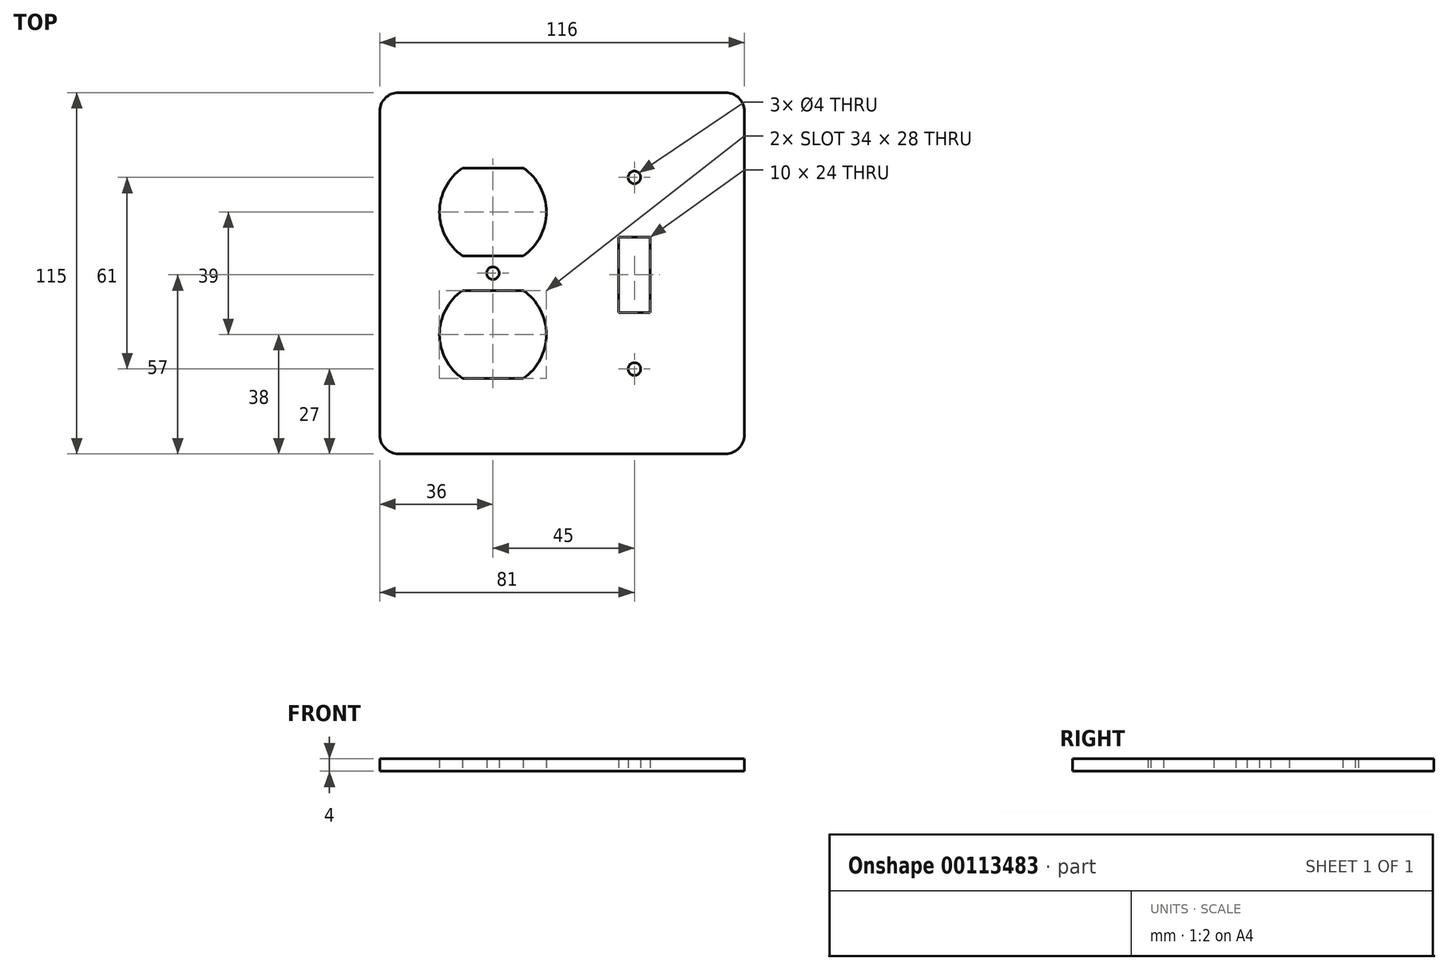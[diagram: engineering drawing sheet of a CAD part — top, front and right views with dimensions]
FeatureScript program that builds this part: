
annotation { "Feature Type Name" : "Feature", "Feature Type Description" : "" }
export const myFeature = defineFeature(function(context is Context, id is Id, definition is map)
    precondition{}
    {
        {
            var Q0;
            Q0=qCreatedBy(makeId("Top.planeOp"),FACE);
            var sketch = newSketch(context, id + "F0", { "sketchPlane" : qUnion([Q0])});
            skLineSegment(sketch, "E0.bottom", {"start": v(0, 0) * mm, "end": v(116, 0) * mm});
            skLineSegment(sketch, "E0.top", {"start": v(0, 115) * mm, "end": v(116, 115) * mm});
            skLineSegment(sketch, "E0.left", {"start": v(0, 0) * mm, "end": v(0, 115) * mm});
            skLineSegment(sketch, "E0.right", {"start": v(116, 0) * mm, "end": v(116, 115) * mm});
            skLineSegment(sketch, "E1.bottom", {"start": v(76, 69) * mm, "end": v(86, 69) * mm});
            skLineSegment(sketch, "E1.top", {"start": v(76, 45) * mm, "end": v(86, 45) * mm});
            skLineSegment(sketch, "E1.left", {"start": v(76, 69) * mm, "end": v(76, 45) * mm});
            skLineSegment(sketch, "E1.right", {"start": v(86, 69) * mm, "end": v(86, 45) * mm});
            skCircle(sketch, "E2", {"center": v(81, 88) * mm, "radius": 2 * mm});
            skCircle(sketch, "E3", {"center": v(81, 27) * mm, "radius": 2 * mm});
            skLineSegment(sketch, "E4.direction1", {"start": v(81, 27) * mm, "end": v(35, 27) * mm, "construction": true});
            skSolve(sketch);
        }
        {
            var Q0;
            Q0=qSketchRegion(id+"F0",true);
            extrude(context, id + "F1", {"entities" : qUnion([Q0]), "depth" : 4 * mm});
        }
        {
            var Q0;
            Q0=makeQuery(id+"F1.opExtrude","SWEPT_EDGE",EDGE,{"disambiguationData":[OSD([sQuery(id+"F0.wireOp",EDGE,"E0.top"),sQuery(id+"F0.wireOp",EDGE,"E0.left")])]});
            var Q1;
            Q1=makeQuery(id+"F1.opExtrude","SWEPT_EDGE",EDGE,{"disambiguationData":[OSD([sQuery(id+"F0.wireOp",EDGE,"E0.top"),sQuery(id+"F0.wireOp",EDGE,"E0.right")])]});
            var Q2;
            Q2=makeQuery(id+"F1.opExtrude","SWEPT_EDGE",EDGE,{"disambiguationData":[OSD([sQuery(id+"F0.wireOp",EDGE,"E0.bottom"),sQuery(id+"F0.wireOp",EDGE,"E0.right")])]});
            var Q3;
            Q3=makeQuery(id+"F1.opExtrude","SWEPT_EDGE",EDGE,{"disambiguationData":[OSD([sQuery(id+"F0.wireOp",EDGE,"E0.bottom"),sQuery(id+"F0.wireOp",EDGE,"E0.left")])]});
            fillet(context, id + "F2", {"entities" : qUnion([Q0, Q1, Q2, Q3]), "radius" : 6 * mm, "tangentPropagation" : true, "allowEdgeOverflow" : false});
        }
        {
            var Q0;
            Q0=makeQuery(id+"F1.opExtrude","CAP_FACE",FACE,{"disambiguationData":[OSD([sQuery(id+"F0.wireOp",EDGE,"E0.bottom"),sQuery(id+"F0.wireOp",EDGE,"E0.top"),sQuery(id+"F0.wireOp",EDGE,"E0.left"),sQuery(id+"F0.wireOp",EDGE,"E0.right"),sQuery(id+"F0.wireOp",EDGE,"E1.bottom"),sQuery(id+"F0.wireOp",EDGE,"E1.top"),sQuery(id+"F0.wireOp",EDGE,"E1.left"),sQuery(id+"F0.wireOp",EDGE,"E1.right"),sQuery(id+"F0.wireOp",EDGE,"E2"),sQuery(id+"F0.wireOp",EDGE,"E3")])],"isStart":false});
            var sketch = newSketch(context, id + "F3", { "sketchPlane" : qUnion([Q0])});
            skLineSegment(sketch, "E5.0.0", {"start": v(0, 109) * mm, "end": v(0, 6) * mm});
            skArc(sketch, "E5.0.1", {"start": v(0, 6) * mm, "mid": v(1.76, 1.76) * mm, "end": v(6, 0) * mm});
            skLineSegment(sketch, "E5.0.2", {"start": v(6, 0) * mm, "end": v(110, 0) * mm});
            skArc(sketch, "E5.0.3", {"start": v(110, 0) * mm, "mid": v(114.24, 1.76) * mm, "end": v(116, 6) * mm});
            skLineSegment(sketch, "E5.0.4", {"start": v(116, 6) * mm, "end": v(116, 109) * mm});
            skArc(sketch, "E5.0.5", {"start": v(116, 109) * mm, "mid": v(114.24, 113.24) * mm, "end": v(110, 115) * mm});
            skLineSegment(sketch, "E5.0.6", {"start": v(110, 115) * mm, "end": v(6, 115) * mm});
            skArc(sketch, "E5.0.7", {"start": v(6, 115) * mm, "mid": v(1.76, 113.24) * mm, "end": v(0, 109) * mm});
            skCircle(sketch, "E6.0", {"center": v(81, 88) * mm, "radius": 2 * mm});
            skLineSegment(sketch, "E7.0", {"start": v(76, 69) * mm, "end": v(86, 69) * mm});
            skLineSegment(sketch, "E8.0", {"start": v(86, 69) * mm, "end": v(86, 45) * mm});
            skLineSegment(sketch, "E9.0", {"start": v(76, 69) * mm, "end": v(76, 45) * mm});
            skLineSegment(sketch, "E10.0", {"start": v(76, 45) * mm, "end": v(86, 45) * mm});
            skCircle(sketch, "E11.0", {"center": v(81, 27) * mm, "radius": 2 * mm});
            skLineSegment(sketch, "E12", {"start": v(81, 69) * mm, "end": v(81, 45) * mm, "construction": true});
            skLineSegment(sketch, "E13", {"start": v(86, 57) * mm, "end": v(76, 57) * mm, "construction": true});
            skPoint(sketch, "E14", {"position": v(81, 57) * mm});
            skSolve(sketch);
        }
        {
            var Q0;
            Q0=qCreatedBy(makeId("Top.planeOp"),FACE);
            var sketch = newSketch(context, id + "F4", { "sketchPlane" : qUnion([Q0])});
            skCircle(sketch, "E15", {"center": v(36, 57.5) * mm, "radius": 2 * mm});
            skCircle(sketch, "E16", {"center": v(36, 77) * mm, "radius": 17 * mm});
            skCircle(sketch, "E17", {"center": v(36, 38) * mm, "radius": 17 * mm});
            skSolve(sketch);
        }
        {
            var Q0;
            Q0=qSketchRegion(id+"F4",true);
            extrude(context, id + "F5", {"entities" : qUnion([Q0]), "operationType" : NewBodyOperationType.REMOVE, "depth" : 25 * mm, "offsetDistance" : 25 * mm});
        }
        {
            var Q0;
            Q0=makeQuery(id+"F3.imprint","IMPRINT",FACE,{"disambiguationData":[TD([[makeQuery(id+"F3.imprint","IMPRINT",EDGE,{"derivedFrom":sQuery(id+"F3.wireOp",EDGE,"E5.0.0")}),-1.0]])]});
            var sketch = newSketch(context, id + "F6", { "sketchPlane" : qUnion([Q0])});
            skLineSegment(sketch, "E18", {"start": v(25.33, 91) * mm, "end": v(46.06, 91) * mm});
            skLineSegment(sketch, "E19", {"start": v(46.06, 91) * mm, "end": v(43.26, 94.42) * mm});
            skLineSegment(sketch, "E20", {"start": v(43.26, 94.42) * mm, "end": v(32.74, 94.84) * mm});
            skLineSegment(sketch, "E21", {"start": v(32.74, 94.84) * mm, "end": v(25.33, 91) * mm});
            skLineSegment(sketch, "E22.bottom", {"start": v(51.19, 59.8) * mm, "end": v(23.64, 59.8) * mm});
            skLineSegment(sketch, "E22.top", {"start": v(51.19, 63) * mm, "end": v(23.64, 63) * mm});
            skLineSegment(sketch, "E22.left", {"start": v(51.19, 59.8) * mm, "end": v(51.19, 63) * mm});
            skLineSegment(sketch, "E22.right", {"start": v(23.64, 59.8) * mm, "end": v(23.64, 63) * mm});
            skLineSegment(sketch, "E23.bottom", {"start": v(22.68, 55.04) * mm, "end": v(51.71, 55.04) * mm});
            skLineSegment(sketch, "E23.top", {"start": v(22.68, 52) * mm, "end": v(51.71, 52) * mm});
            skLineSegment(sketch, "E23.left", {"start": v(22.68, 55.04) * mm, "end": v(22.68, 52) * mm});
            skLineSegment(sketch, "E23.right", {"start": v(51.71, 55.04) * mm, "end": v(51.71, 52) * mm});
            skLineSegment(sketch, "E24.bottom", {"start": v(20.13, 24) * mm, "end": v(53.35, 24) * mm});
            skLineSegment(sketch, "E24.top", {"start": v(20.13, 21) * mm, "end": v(53.35, 21) * mm});
            skLineSegment(sketch, "E24.left", {"start": v(20.13, 24) * mm, "end": v(20.13, 21) * mm});
            skLineSegment(sketch, "E24.right", {"start": v(53.35, 24) * mm, "end": v(53.35, 21) * mm});
            skSolve(sketch);
        }
        {
            var Q0;
            Q0=qSketchRegion(id+"F6",true);
            extrude(context, id + "F7", {"entities" : qUnion([Q0]), "operationType" : NewBodyOperationType.ADD, "oppositeDirection" : true, "depth" : 4 * mm, "offsetDistance" : 25 * mm});
        }
    });
